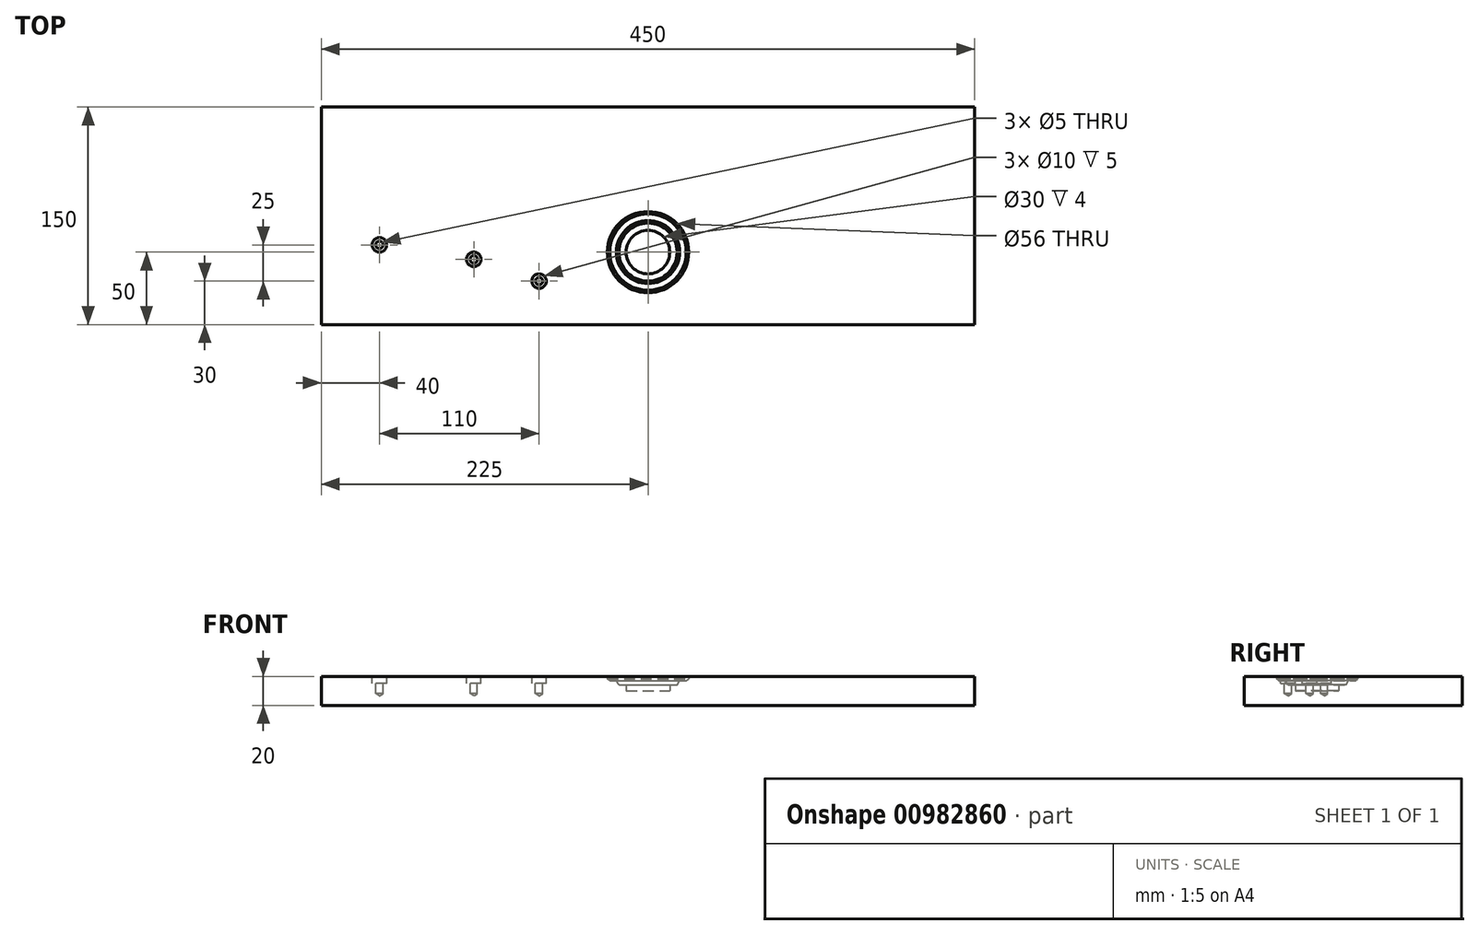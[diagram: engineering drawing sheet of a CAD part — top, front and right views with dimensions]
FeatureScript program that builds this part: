
annotation { "Feature Type Name" : "Feature", "Feature Type Description" : "" }
export const myFeature = defineFeature(function(context is Context, id is Id, definition is map)
    precondition{}
    {
        {
            var Q0;
            Q0=qCreatedBy(makeId("Right.planeOp"),FACE);
            var sketch = newSketch(context, id + "F0", { "sketchPlane" : qUnion([Q0])});
            skLineSegment(sketch, "E0.bottom", {"start": v(75, 10) * mm, "end": v(-75, 10) * mm});
            skLineSegment(sketch, "E0.top", {"start": v(75, -10) * mm, "end": v(-75, -10) * mm});
            skLineSegment(sketch, "E0.left", {"start": v(75, 10) * mm, "end": v(75, -10) * mm});
            skLineSegment(sketch, "E0.right", {"start": v(-75, 10) * mm, "end": v(-75, -10) * mm});
            skPoint(sketch, "E0.middle", {"position": v(0, 0) * mm});
            skSolve(sketch);
        }
        {
            var Q0;
            Q0=makeQuery(id+"F0.imprint","IMPRINT",FACE,{"disambiguationData":[TD([[makeQuery(id+"F0.imprint","IMPRINT",EDGE,{"derivedFrom":sQuery(id+"F0.wireOp",EDGE,"E0.bottom")}),1.0]])]});
            extrude(context, id + "F1", {"entities" : qUnion([Q0]), "endBound" : BoundingType.SYMMETRIC, "depth" : 450 * mm, "offsetDistance" : 25 * mm});
        }
        {
            var Q0;
            Q0=makeQuery(id+"F1.opExtrude","SWEPT_FACE",FACE,{"disambiguationData":[OSD([sQuery(id+"F0.wireOp",EDGE,"E0.bottom")])]});
            var sketch = newSketch(context, id + "F2", { "sketchPlane" : qUnion([Q0])});
            skPoint(sketch, "E1", {"position": v(-185, -20) * mm});
            skPoint(sketch, "E2", {"position": v(-120, -30) * mm});
            skPoint(sketch, "E3", {"position": v(-75, -45) * mm});
            skSolve(sketch);
        }
        {
            var Q0;
            Q0=sQuery(id+"F2.wireOp",VERTEX,"E3");
            var Q1;
            Q1=sQuery(id+"F2.wireOp",VERTEX,"E2");
            var Q2;
            Q2=sQuery(id+"F2.wireOp",VERTEX,"E1");
            var Q3;
            Q3=makeQuery(id+"F1.opExtrude","SWEPT_BODY",BODY,{"disambiguationData":[OSD([sQuery(id+"F0.wireOp",EDGE,"E0.bottom"),sQuery(id+"F0.wireOp",EDGE,"E0.top"),sQuery(id+"F0.wireOp",EDGE,"E0.left"),sQuery(id+"F0.wireOp",EDGE,"E0.right")])]});
            hole(context, id + "F3", {"style" : HoleStyle.C_BORE, "endStyle" : HoleEndStyle.BLIND, "holeDiameter" : 5 * mm, "cBoreDiameter" : 10 * mm, "cBoreDepth" : 5 * mm, "majorDiameter" : 5 * mm, "holeDepth" : 12 * mm, "isTappedThrough" : true, "tappedDepth" : 12 * mm, "tapClearance" : 3, "locations" : qUnion([Q0, Q1, Q2]), "scope" : qUnion([Q3])});
        }
        {
            var Q0;
            Q0=qCreatedBy(makeId("Front.planeOp"),FACE);
            cPlane(context, id + "F4", {"entities" : qUnion([Q0]), "cplaneType" : CPlaneType.OFFSET, "offset" : 25 * mm, "width" : 150 * mm, "height" : 150 * mm});
        }
        {
            var Q0;
            Q0=qCreatedBy(id+"F4.planeOp",FACE);
            var sketch = newSketch(context, id + "F5", { "sketchPlane" : qUnion([Q0])});
            skLineSegment(sketch, "E4", {"start": v(0, 0) * mm, "end": v(15, 0) * mm});
            skLineSegment(sketch, "E5", {"start": v(15, 0) * mm, "end": v(15, 4) * mm});
            skLineSegment(sketch, "E6", {"start": v(15, 4) * mm, "end": v(20, 4) * mm});
            skLineSegment(sketch, "E7", {"start": v(20, 4) * mm, "end": v(21.73, 7) * mm});
            skLineSegment(sketch, "E8", {"start": v(21.73, 7) * mm, "end": v(26.29, 7) * mm});
            skLineSegment(sketch, "E9", {"start": v(26.29, 7) * mm, "end": v(28, 8.2) * mm});
            skLineSegment(sketch, "E10", {"start": v(28, 8.2) * mm, "end": v(28, 10) * mm});
            skLineSegment(sketch, "E11", {"start": v(28, 10) * mm, "end": v(0, 10) * mm});
            skLineSegment(sketch, "E12", {"start": v(0, 10) * mm, "end": v(0, 0) * mm});
            skSolve(sketch);
        }
        {
            var Q0;
            Q0 = qSketchRegion(id + "F5", true);
            var Q1;
            Q1=sQuery(id+"F5.wireOp",EDGE,"E12");
            revolve(context, id + "F6", {"operationType" : NewBodyOperationType.REMOVE, "surfaceOperationType" : NewSurfaceOperationType.NEW, "entities" : qUnion([Q0]), "axis" : qUnion([Q1]), "revolveType" : RevolveType.FULL, "oppositeDirection" : true});
        }
    });
